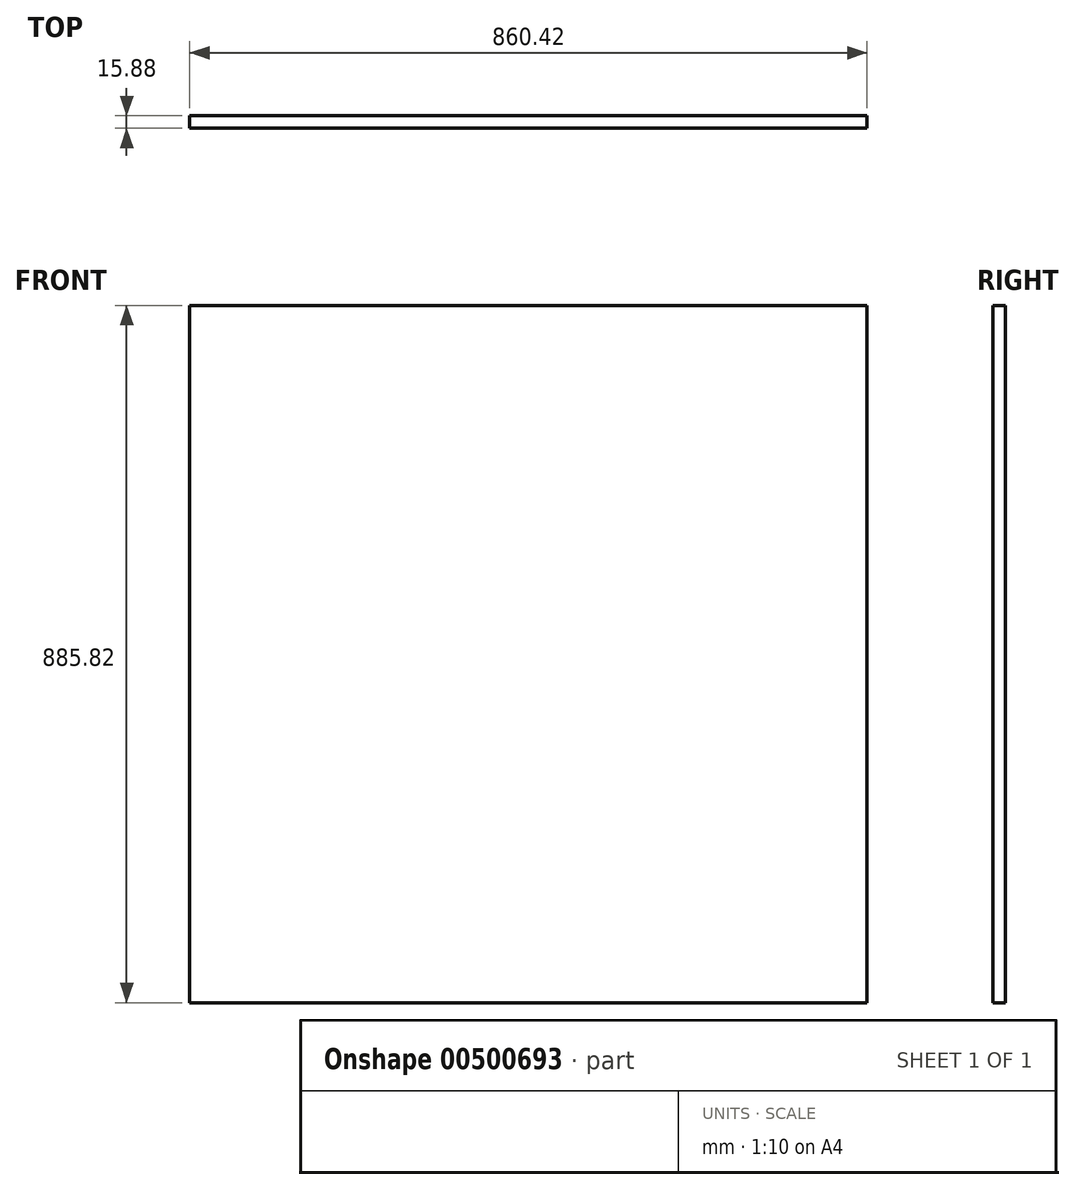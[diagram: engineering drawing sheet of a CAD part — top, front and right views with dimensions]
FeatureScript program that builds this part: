
annotation { "Feature Type Name" : "Feature", "Feature Type Description" : "" }
export const myFeature = defineFeature(function(context is Context, id is Id, definition is map)
    precondition{}
    {
        {
            var Q0;
            Q0=qCreatedBy(makeId("Front.planeOp"),FACE);
            var sketch = newSketch(context, id + "F0", { "sketchPlane" : qUnion([Q0])});
            skLineSegment(sketch, "E0.bottom", {"start": v(0, 0) * mm, "end": v(860.42, 0) * mm});
            skLineSegment(sketch, "E0.top", {"start": v(0, 885.82) * mm, "end": v(860.42, 885.82) * mm});
            skLineSegment(sketch, "E0.left", {"start": v(0, 0) * mm, "end": v(0, 885.82) * mm});
            skLineSegment(sketch, "E0.right", {"start": v(860.43, 0) * mm, "end": v(860.42, 885.82) * mm});
            skSolve(sketch);
        }
        {
            var Q0;
            Q0=makeQuery(id+"F0.imprint","IMPRINT",FACE,{"disambiguationData":[TD([[makeQuery(id+"F0.imprint","IMPRINT",EDGE,{"derivedFrom":sQuery(id+"F0.wireOp",EDGE,"E0.bottom")}),1.0]])]});
            extrude(context, id + "F1", {"entities" : qUnion([Q0]), "oppositeDirection" : true, "depth" : 15.88 * mm, "offsetDistance" : 25.4 * mm});
        }
    });
